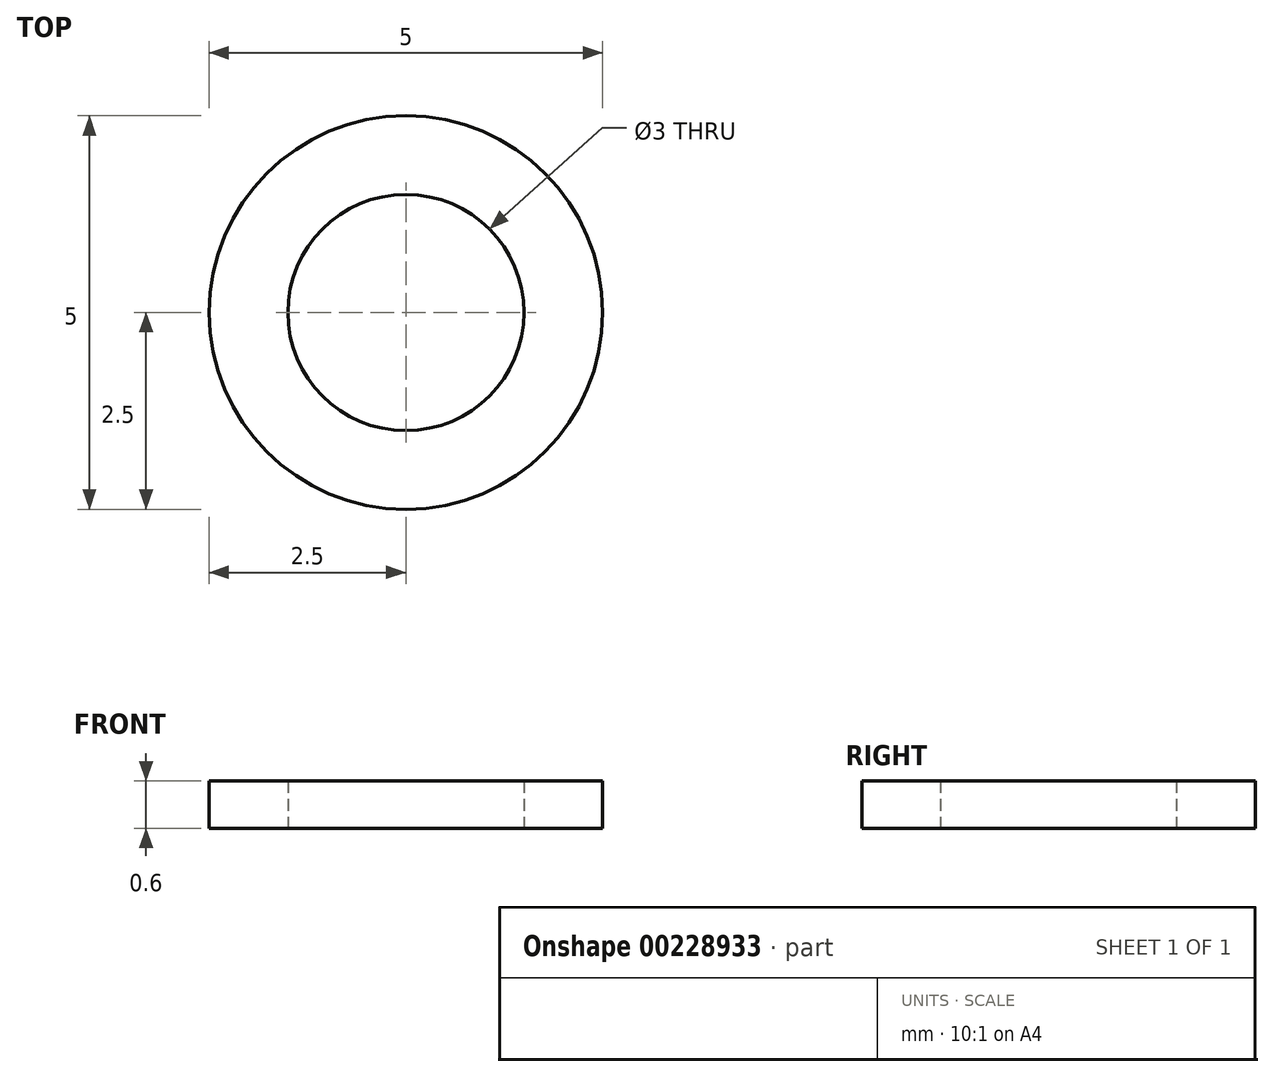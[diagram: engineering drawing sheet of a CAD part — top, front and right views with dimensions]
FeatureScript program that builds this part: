
annotation { "Feature Type Name" : "Feature", "Feature Type Description" : "" }
export const myFeature = defineFeature(function(context is Context, id is Id, definition is map)
    precondition{}
    {
        {
            var Q0;
            Q0=qCreatedBy(makeId("Top.planeOp"),FACE);
            var sketch = newSketch(context, id + "F0", { "sketchPlane" : qUnion([Q0])});
            skCircle(sketch, "E0", {"center": v(0, 0) * mm, "radius": 2.5 * mm});
            skCircle(sketch, "E1", {"center": v(0, 0) * mm, "radius": 1.5 * mm});
            skSolve(sketch);
        }
        {
            var Q0;
            Q0 = qSketchRegion(id + "F0", true);
            extrude(context, id + "F1", {"entities" : qUnion([Q0]), "depth" : 0.6 * mm});
        }
    });
